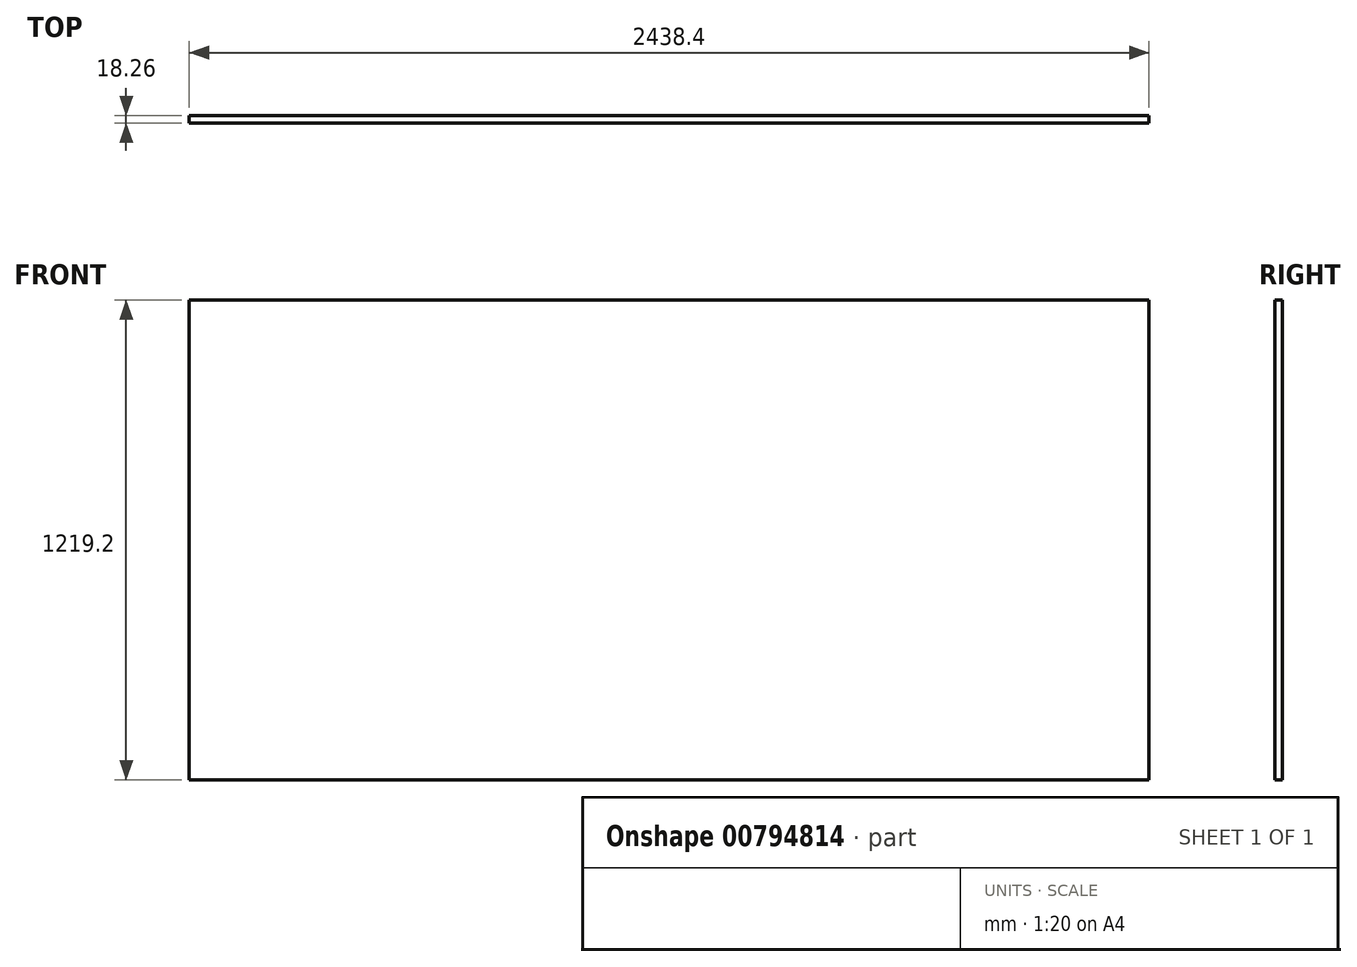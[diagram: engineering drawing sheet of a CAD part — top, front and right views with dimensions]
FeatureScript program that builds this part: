
annotation { "Feature Type Name" : "Feature", "Feature Type Description" : "" }
export const myFeature = defineFeature(function(context is Context, id is Id, definition is map)
    precondition{}
    {
        {
            var Q0;
            Q0=qCreatedBy(makeId("Front.planeOp"),FACE);
            var sketch = newSketch(context, id + "F0", { "sketchPlane" : qUnion([Q0])});
            skLineSegment(sketch, "E0.bottom", {"start": v(-1207.9, 596.48) * mm, "end": v(1230.5, 596.48) * mm});
            skLineSegment(sketch, "E0.top", {"start": v(-1207.9, -622.72) * mm, "end": v(1230.5, -622.72) * mm});
            skLineSegment(sketch, "E0.left", {"start": v(-1207.9, 596.48) * mm, "end": v(-1207.9, -622.72) * mm});
            skLineSegment(sketch, "E0.right", {"start": v(1230.5, 596.48) * mm, "end": v(1230.5, -622.72) * mm});
            skSolve(sketch);
        }
        {
            var Q0;
            Q0 = qSketchRegion(id + "F0", true);
            extrude(context, id + "F1", {"entities" : qUnion([Q0]), "depth" : 18.26 * mm, "offsetDistance" : 25.4 * mm});
        }
    });
